# Revit family: Поли-Групп_ЗадвижкаКлиноваяEAZ-МК-F3(ВS)_DN350-1600
name_source: partatom
category: Арматура трубопроводов
units: mm (PartAtom-declared; Revit-internal decimal feet)

## family parameters
Всегда вертикально = Да
На основе рабочей плоскости = Нет
Общий = Нет
При загрузке вырезать с полостями = Нет
Размер круглого соединителя = Использовать диаметр
Тип детали = Клапан - Вставляется

## types (24) — shared parameters
ADSK_URL страницы изделия = https://www.polycorr.ru
ADSK_Версия Revit = 2019
ADSK_Единица измерения = шт
ADSK_Завод-изготовитель = ООО ПК «Поли-Групп»
ADSK_Количество = 1
ADSK_Материал = Высокопрочный чугун GGG-40
ADSK_Материал наименование = Высокопрочный чугун с шаровидным графитом (GGG-40)
Kv = 1.0 м³/ч
Класс герметичности = А по ГОСТ Р 9544-2015
Материал Диска = Высокопрочный чугун с шаровидным графитом (GGG-40)
Материал уплотнителя = PTFE
Назначение = Для установки в качестве запорного устройства на трубопроводах
Покрытие = Высококачественное эпоксидное покрытие толщиной 300 мкм
Рабочая среда = Техническая вода, канализационные стоки, морская вода
Разработчик = https://3dbim.pro
Срок службы = 50 лет
ТВ = Поли-Групп_ЗадвижкаКлиноваяEAZ-МК-F3(ВS)_DN350-1600
Температура рабочей среды = 0 до +70°С
Тип привода = Редуктор
Тип присоединения = Фланцевое

## per-type parameters (varying)
- 350-10: A=756 мм; ADSK_Марка=EAZ-GV-1-F3 DN350 PN10; ADSK_Масса=225; ADSK_Масса_Текст=225; ADSK_Наименование=Задвижка клиновая с металлическим уплотнением EAZ MK F3 для сточных вод фланцевая DN350 PN10; ADSK_Наименование краткое=Задвижка клиновая EAZ MK F3 DN350 PN10; D=505 мм; D1=460 мм; D2=429 мм; DN=350 мм; D_Наружный=359 мм; H1=270 мм; H2=976 мм; L=381 мм; L1=270 мм; L2=81 мм; PN=10.0 бары; R=21 мм; R1=206 мм; b=25 мм; d1=88 мм; f=4 мм; h2=683 мм; l1=229 мм; l2=248 мм; l3=343 мм; t=68 мм; Габаритные размеры=505х381х1246; Корпус_Глубина=605 мм; с=18 мм
- 400-10: A=836 мм; ADSK_Марка=EAZ-GV-1-F3 DN400 PN10; ADSK_Масса=292; ADSK_Масса_Текст=292; ADSK_Наименование=Задвижка клиновая с металлическим уплотнением EAZ MK F3 для сточных вод фланцевая DN400 PN10; ADSK_Наименование краткое=Задвижка клиновая EAZ MK F3 DN400 PN10; D=565 мм; D1=515 мм; D2=480 мм; DN=400 мм; D_Наружный=409 мм; H1=300 мм; H2=1068 мм; L=406 мм; L1=300 мм; L2=90 мм; PN=10.0 бары; R=21 мм; R1=206 мм; b=25 мм; d1=100 мм; f=4 мм; h2=748 мм; l1=244 мм; l2=264 мм; l3=365 мм; t=75 мм; Габаритные размеры=565х406х1368; Корпус_Глубина=669 мм; с=18 мм
- 450-10: A=916 мм; ADSK_Марка=EAZ-GV-1-F3  DN450 PN10; ADSK_Масса=398; ADSK_Масса_Текст=398; ADSK_Наименование=Задвижка клиновая с металлическим уплотнением EAZ MK F3 для сточных вод фланцевая DN450 PN10; ADSK_Наименование краткое=Задвижка клиновая EAZ MK F3 DN450 PN10; D=615 мм; D1=565 мм; D2=530 мм; DN=450 мм; D_Наружный=459 мм; H1=330 мм; H2=1180 мм; L=432 мм; L1=330 мм; L2=99 мм; PN=10.0 бары; R=28 мм; R1=275 мм; b=26 мм; d1=113 мм; f=4 мм; h2=826 мм; l1=259 мм; l2=281 мм; l3=389 мм; t=83 мм; Габаритные размеры=615х432х1510; Корпус_Глубина=733 мм; с=23 мм
- 500-10: A=996 мм; ADSK_Марка=EAZ-GV-1-F3 DN500 PN10; ADSK_Масса=470; ADSK_Масса_Текст=470; ADSK_Наименование=Задвижка клиновая с металлическим уплотнением EAZ MK F3 для сточных вод фланцевая DN500 PN10; ADSK_Наименование краткое=Задвижка клиновая EAZ MK F3 DN500 PN10; D=670 мм; D1=620 мм; D2=582 мм; DN=500 мм; D_Наружный=509 мм; H1=370 мм; H2=1247 мм; L=457 мм; L1=370 мм; L2=111 мм; PN=10.0 бары; R=28 мм; R1=275 мм; b=27 мм; d1=125 мм; f=4 мм; h2=873 мм; l1=274 мм; l2=297 мм; l3=411 мм; t=87 мм; Габаритные размеры=670х457х1617; Корпус_Глубина=797 мм; с=35 мм
- 600-10: A=1076 мм; ADSK_Марка=EAZ-GV-1-F3 DN600 PN10; ADSK_Масса=705; ADSK_Масса_Текст=705; ADSK_Наименование=Задвижка клиновая с металлическим уплотнением EAZ MK F3 для сточных вод фланцевая DN600 PN10; ADSK_Наименование краткое=Задвижка клиновая EAZ MK F3 DN600 PN10; D=780 мм; D1=725 мм; D2=682 мм; DN=600 мм; D_Наружный=609 мм; H1=430 мм; H2=1416 мм; L=508 мм; L1=430 мм; L2=129 мм; PN=10.0 бары; R=28 мм; R1=275 мм; b=30 мм; d1=150 мм; f=5 мм; h2=991 мм; l1=305 мм; l2=330 мм; l3=457 мм; t=99 мм; Габаритные размеры=780х508х1846; Корпус_Глубина=861 мм; с=40 мм
- 700-10: A=1156 мм; ADSK_Марка=EAZ-GV-1-F3 DN700 PN10; ADSK_Масса=1503; ADSK_Масса_Текст=1503; ADSK_Наименование=Задвижка клиновая с металлическим уплотнением EAZ MK F3 для сточных вод фланцевая DN700 PN10; ADSK_Наименование краткое=Задвижка клиновая EAZ MK F3 DN700 PN10; D=895 мм; D1=840 мм; D2=794 мм; DN=700 мм; D_Наружный=709 мм; H1=495 мм; H2=1808 мм; L=610 мм; L1=495 мм; L2=149 мм; PN=10.0 бары; R=31 мм; R1=307 мм; b=33 мм; d1=175 мм; f=5 мм; h2=1266 мм; l1=366 мм; l2=397 мм; l3=549 мм; t=127 мм; Габаритные размеры=895х610х2303; Корпус_Глубина=925 мм; с=48 мм
- 800-10: A=1242 мм; ADSK_Марка=EAZ-GV-1-F3 DN800 PN10; ADSK_Масса=2125; ADSK_Масса_Текст=2125; ADSK_Наименование=Задвижка клиновая с металлическим уплотнением EAZ MK F3 для сточных вод фланцевая DN800 PN10; ADSK_Наименование краткое=Задвижка клиновая EAZ MK F3 DN800 PN10; D=1015 мм; D1=950 мм; D2=901 мм; DN=800 мм; D_Наружный=809 мм; H1=540 мм; H2=1953 мм; L=660 мм; L1=540 мм; L2=162 мм; PN=10.0 бары; R=33 мм; R1=330 мм; b=35 мм; d1=200 мм; f=5 мм; h2=1367 мм; l1=396 мм; l2=429 мм; l3=594 мм; t=137 мм; Габаритные размеры=1015х660х2493; Корпус_Глубина=994 мм; с=33 мм
- 900-10: A=1423 мм; ADSK_Марка=EAZ-GV-1-F3 DN900 PN10; ADSK_Масса=2750; ADSK_Масса_Текст=2750; ADSK_Наименование=Задвижка клиновая с металлическим уплотнением EAZ MK F3 для сточных вод фланцевая DN900 PN10; ADSK_Наименование краткое=Задвижка клиновая EAZ MK F3 DN900 PN10; D=1115 мм; D1=1050 мм; D2=1001 мм; DN=900 мм; D_Наружный=909 мм; H1=645 мм; H2=2132 мм; L=711 мм; L1=600 мм; L2=180 мм; PN=10.0 бары; R=37 мм; R1=370 мм; b=38 мм; d1=225 мм; f=5 мм; h2=1492 мм; l1=427 мм; l2=462 мм; l3=640 мм; t=149 мм; Габаритные размеры=1115х711х2777; Корпус_Глубина=1138 мм; с=88 мм
- 1000-10: A=1448 мм; ADSK_Марка=EAZ-GV-1-F3 DN1000 PN10; ADSK_Масса=3310; ADSK_Масса_Текст=3310; ADSK_Наименование=Задвижка клиновая с металлическим уплотнением EAZ MK F3 для сточных вод фланцевая DN1000 PN10; ADSK_Наименование краткое=Задвижка клиновая EAZ MK F3 DN1000 PN10; D=1230 мм; D1=1160 мм; D2=1112 мм; DN=1000 мм; D_Наружный=1009 мм; H1=680 мм; H2=2362 мм; L=811 мм; L1=680 мм; L2=204 мм; PN=10.0 бары; R=39 мм; R1=390 мм; b=40 мм; d1=250 мм; f=5 мм; h2=1653 мм; l1=487 мм; l2=527 мм; l3=730 мм; t=165 мм; Габаритные размеры=1230х811х3042; Корпус_Глубина=1158 мм; с=65 мм
- 1200-10: A=1625 мм; ADSK_Марка=EAZ-GV-1-F3 DN1200 PN10; ADSK_Масса=4970; ADSK_Масса_Текст=4970; ADSK_Наименование=Задвижка клиновая с металлическим уплотнением EAZ MK F3 для сточных вод фланцевая DN1200 PN10; ADSK_Наименование краткое=Задвижка клиновая EAZ MK F3 DN1200 PN10; D=1455 мм; D1=1380 мм; D2=1328 мм; DN=1200 мм; D_Наружный=1209 мм; H1=800 мм; H2=2652 мм; L=960 мм; L1=800 мм; L2=240 мм; PN=10.0 бары; R=43 мм; R1=430 мм; b=45 мм; d1=300 мм; f=5 мм; h2=1856 мм; l1=576 мм; l2=624 мм; l3=864 мм; t=186 мм; Габаритные размеры=1455х960х3452; Корпус_Глубина=1300 мм; с=73 мм
- 1400-10: A=1860 мм; ADSK_Марка=EAZ-GV-1-F3 DN1400 PN10; ADSK_Масса=6790; ADSK_Масса_Текст=6790; ADSK_Наименование=Задвижка клиновая с металлическим уплотнением EAZ MK F3 для сточных вод фланцевая DN1400 PN10; ADSK_Наименование краткое=Задвижка клиновая EAZ MK F3 DN1400 PN10; D=1675 мм; D1=1590 мм; D2=1530 мм; DN=1400 мм; D_Наружный=1409 мм; H1=870 мм; H2=2972 мм; L=960 мм; L1=870 мм; L2=261 мм; PN=10.0 бары; R=51 мм; R1=510 мм; b=46 мм; d1=350 мм; f=5 мм; h2=2080 мм; l1=576 мм; l2=624 мм; l3=864 мм; t=208 мм; Габаритные размеры=1675х960х3842; Корпус_Глубина=1488 мм; с=33 мм
- 1600-10: A=2065 мм; ADSK_Марка=EAZ-GV-1-F3 DN1600 PN10; ADSK_Масса=9580; ADSK_Масса_Текст=9580; ADSK_Наименование=Задвижка клиновая с металлическим уплотнением EAZ MK F3 для сточных вод фланцевая DN1600 PN10; ADSK_Наименование краткое=Задвижка клиновая EAZ MK F3 DN1600 PN10; D=1915 мм; D1=1820 мм; D2=1750 мм; DN=1600 мм; D_Наружный=1609 мм; H1=1000 мм; H2=3380 мм; L=1140 мм; L1=1000 мм; L2=300 мм; PN=10.0 бары; R=63 мм; R1=630 мм; b=49 мм; d1=400 мм; f=5 мм; h2=2366 мм; l1=684 мм; l2=741 мм; l3=1026 мм; t=237 мм; Габаритные размеры=1915х1140х4380; Корпус_Глубина=1652 мм; с=43 мм
- 350-16: A=756 мм; ADSK_Марка=EAZ-GV-1-F3 DN350 PN16; ADSK_Масса=228; ADSK_Масса_Текст=228; ADSK_Наименование=Задвижка клиновая с металлическим уплотнением EAZ MK F3 для сточных вод фланцевая DN350 PN16; ADSK_Наименование краткое=Задвижка клиновая EAZ MK F3 DN350 PN16; D=520 мм; D1=470 мм; D2=429 мм; DN=350 мм; D_Наружный=359 мм; H1=270 мм; H2=976 мм; L=381 мм; L1=270 мм; L2=81 мм; PN=16.0 бары; R=21 мм; R1=206 мм; b=27 мм; d1=88 мм; f=4 мм; h2=683 мм; l1=229 мм; l2=248 мм; l3=343 мм; t=68 мм; Габаритные размеры=520х381х1246; Корпус_Глубина=605 мм; с=10 мм
- 400-16: A=836 мм; ADSK_Марка=EAZ-GV-1-F3 DN400 PN16; ADSK_Масса=299; ADSK_Масса_Текст=299; ADSK_Наименование=Задвижка клиновая с металлическим уплотнением EAZ MK F3 для сточных вод фланцевая DN400 PN16; ADSK_Наименование краткое=Задвижка клиновая EAZ MK F3 DN400 PN16; D=580 мм; D1=525 мм; D2=480 мм; DN=400 мм; D_Наружный=409 мм; H1=300 мм; H2=1068 мм; L=406 мм; L1=300 мм; L2=90 мм; PN=16.0 бары; R=21 мм; R1=206 мм; b=28 мм; d1=100 мм; f=4 мм; h2=748 мм; l1=244 мм; l2=264 мм; l3=365 мм; t=75 мм; Габаритные размеры=580х406х1368; Корпус_Глубина=669 мм; с=10 мм
- 450-16: A=916 мм; ADSK_Марка=EAZ-GV-1-F3 DN450 PN16; ADSK_Масса=405; ADSK_Масса_Текст=405; ADSK_Наименование=Задвижка клиновая с металлическим уплотнением EAZ MK F3 для сточных вод фланцевая DN450 PN16; ADSK_Наименование краткое=Задвижка клиновая EAZ MK F3 DN450 PN16; D=640 мм; D1=585 мм; D2=548 мм; DN=450 мм; D_Наружный=459 мм; H1=330 мм; H2=1180 мм; L=432 мм; L1=330 мм; L2=99 мм; PN=16.0 бары; R=28 мм; R1=275 мм; b=30 мм; d1=113 мм; f=4 мм; h2=826 мм; l1=259 мм; l2=281 мм; l3=389 мм; t=83 мм; Габаритные размеры=640х432х1510; Корпус_Глубина=733 мм; с=10 мм
- 500-16: A=996 мм; ADSK_Марка=EAZ-GV-1-F3 DN500 PN16; ADSK_Масса=480; ADSK_Масса_Текст=480; ADSK_Наименование=Задвижка клиновая с металлическим уплотнением EAZ MK F3 для сточных вод фланцевая DN500 PN16; ADSK_Наименование краткое=Задвижка клиновая EAZ MK F3 DN500 PN16; D=715 мм; D1=650 мм; D2=609 мм; DN=500 мм; D_Наружный=509 мм; H1=370 мм; H2=1247 мм; L=457 мм; L1=370 мм; L2=111 мм; PN=16.0 бары; R=28 мм; R1=275 мм; b=32 мм; d1=125 мм; f=4 мм; h2=873 мм; l1=274 мм; l2=297 мм; l3=411 мм; t=87 мм; Габаритные размеры=715х457х1617; Корпус_Глубина=797 мм; с=13 мм
- 600-16: A=1076 мм; ADSK_Марка=EAZ-GV-1-F3 DN600 PN16; ADSK_Масса=718; ADSK_Масса_Текст=718; ADSK_Наименование=Задвижка клиновая с металлическим уплотнением EAZ MK F3 для сточных вод фланцевая DN600 PN16; ADSK_Наименование краткое=Задвижка клиновая EAZ MK F3 DN600 PN16; D=840 мм; D1=770 мм; D2=720 мм; DN=600 мм; D_Наружный=609 мм; H1=430 мм; H2=1416 мм; L=508 мм; L1=430 мм; L2=129 мм; PN=16.0 бары; R=28 мм; R1=275 мм; b=36 мм; d1=150 мм; f=5 мм; h2=991 мм; l1=305 мм; l2=330 мм; l3=457 мм; t=99 мм; Габаритные размеры=840х508х1846; Корпус_Глубина=861 мм; с=10 мм
- 700-16: A=1156 мм; ADSK_Марка=EAZ-GV-1-F3 DN700 PN16; ADSK_Масса=1545; ADSK_Масса_Текст=1545; ADSK_Наименование=Задвижка клиновая с металлическим уплотнением EAZ MK F3 для сточных вод фланцевая DN700 PN16; ADSK_Наименование краткое=Задвижка клиновая EAZ MK F3 DN700 PN16; D=910 мм; D1=840 мм; D2=794 мм; DN=700 мм; D_Наружный=709 мм; H1=495 мм; H2=1808 мм; L=610 мм; L1=495 мм; L2=149 мм; PN=16.0 бары; R=31 мм; R1=307 мм; b=40 мм; d1=175 мм; f=5 мм; h2=1266 мм; l1=366 мм; l2=397 мм; l3=549 мм; t=127 мм; Габаритные размеры=910х610х2303; Корпус_Глубина=925 мм; с=40 мм
- 800-16: A=1242 мм; ADSK_Марка=EAZ-GV-1-F3 DN800 PN16; ADSK_Масса=2140; ADSK_Масса_Текст=2140; ADSK_Наименование=Задвижка клиновая с металлическим уплотнением EAZ MK F3 для сточных вод фланцевая DN800 PN16; ADSK_Наименование краткое=Задвижка клиновая EAZ MK F3 DN800 PN16; D=1025 мм; D1=950 мм; D2=901 мм; DN=800 мм; D_Наружный=809 мм; H1=540 мм; H2=1953 мм; L=660 мм; L1=540 мм; L2=162 мм; PN=16.0 бары; R=33 мм; R1=330 мм; b=43 мм; d1=200 мм; f=5 мм; h2=1367 мм; l1=396 мм; l2=429 мм; l3=594 мм; t=137 мм; Габаритные размеры=1025х660х2493; Корпус_Глубина=994 мм; с=28 мм
- 900-16: A=1423 мм; ADSK_Марка=EAZ-GV-1-F3 DN900 PN16; ADSK_Масса=2900; ADSK_Масса_Текст=2900; ADSK_Наименование=Задвижка клиновая с металлическим уплотнением EAZ MK F3 для сточных вод фланцевая DN900 PN16; ADSK_Наименование краткое=Задвижка клиновая EAZ MK F3 DN900 PN16; D=1125 мм; D1=1050 мм; D2=1001 мм; DN=900 мм; D_Наружный=909 мм; H1=645 мм; H2=2132 мм; L=711 мм; L1=600 мм; L2=180 мм; PN=16.0 бары; R=37 мм; R1=370 мм; b=47 мм; d1=225 мм; f=5 мм; h2=1492 мм; l1=427 мм; l2=462 мм; l3=640 мм; t=149 мм; Габаритные размеры=1125х711х2777; Корпус_Глубина=1138 мм; с=83 мм
- 1000-16: A=1448 мм; ADSK_Марка=EAZ-GV-1-F3 DN1000 PN16; ADSK_Масса=3380; ADSK_Масса_Текст=3380; ADSK_Наименование=Задвижка клиновая с металлическим уплотнением EAZ MK F3 для сточных вод фланцевая DN1000 PN16; ADSK_Наименование краткое=Задвижка клиновая EAZ MK F3 DN1000 PN16; D=1255 мм; D1=1170 мм; D2=1112 мм; DN=1000 мм; D_Наружный=1009 мм; H1=680 мм; H2=2362 мм; L=811 мм; L1=680 мм; L2=204 мм; PN=16.0 бары; R=39 мм; R1=390 мм; b=50 мм; d1=250 мм; f=5 мм; h2=1653 мм; l1=487 мм; l2=527 мм; l3=730 мм; t=165 мм; Габаритные размеры=1255х811х3042; Корпус_Глубина=1158 мм; с=53 мм
- 1200-16: A=1625 мм; ADSK_Марка=EAZ-GV-1-F3 DN1200 PN16; ADSK_Масса=5000; ADSK_Масса_Текст=5000; ADSK_Наименование=Задвижка клиновая с металлическим уплотнением EAZ MK F3 для сточных вод фланцевая DN1200 PN16; ADSK_Наименование краткое=Задвижка клиновая EAZ MK F3 DN1200 PN16; D=1485 мм; D1=1390 мм; D2=1328 мм; DN=1200 мм; D_Наружный=1209 мм; H1=825 мм; H2=2652 мм; L=960 мм; L1=825 мм; L2=248 мм; PN=16.0 бары; R=43 мм; R1=430 мм; b=57 мм; d1=300 мм; f=5 мм; h2=1856 мм; l1=576 мм; l2=624 мм; l3=864 мм; t=186 мм; Габаритные размеры=1485х960х3477; Корпус_Глубина=1300 мм; с=83 мм
- 1400-16: A=1860 мм; ADSK_Марка=EAZ-GV-1-F3 DN1400 PN16; ADSK_Масса=7040; ADSK_Масса_Текст=7040; ADSK_Наименование=Задвижка клиновая с металлическим уплотнением EAZ MK F3 для сточных вод фланцевая DN1400 PN16; ADSK_Наименование краткое=Задвижка клиновая EAZ MK F3 DN1400 PN16; D=1685 мм; D1=1590 мм; D2=1530 мм; DN=1400 мм; D_Наружный=1409 мм; H1=870 мм; H2=3010 мм; L=960 мм; L1=870 мм; L2=261 мм; PN=16.0 бары; R=51 мм; R1=510 мм; b=60 мм; d1=350 мм; f=5 мм; h2=2107 мм; l1=576 мм; l2=624 мм; l3=864 мм; t=211 мм; Габаритные размеры=1685х960х3880; Корпус_Глубина=1488 мм; с=28 мм
- 1600-16: A=2065 мм; ADSK_Марка=EAZ-GV-1-F3 DN1600 PN16; ADSK_Масса=9750; ADSK_Масса_Текст=9750; ADSK_Наименование=Задвижка клиновая с металлическим уплотнением EAZ MK F3 для сточных вод фланцевая DN1600 PN16; ADSK_Наименование краткое=Задвижка клиновая EAZ MK F3 DN1600 PN16; D=1930 мм; D1=1820 мм; D2=1750 мм; DN=1600 мм; D_Наружный=1609 мм; H1=1000 мм; H2=3410 мм; L=1140 мм; L1=1000 мм; L2=300 мм; PN=16.0 бары; R=63 мм; R1=630 мм; b=65 мм; d1=400 мм; f=5 мм; h2=2387 мм; l1=684 мм; l2=741 мм; l3=1026 мм; t=239 мм; Габаритные размеры=1930х1140х4410; Корпус_Глубина=1652 мм; с=35 мм
